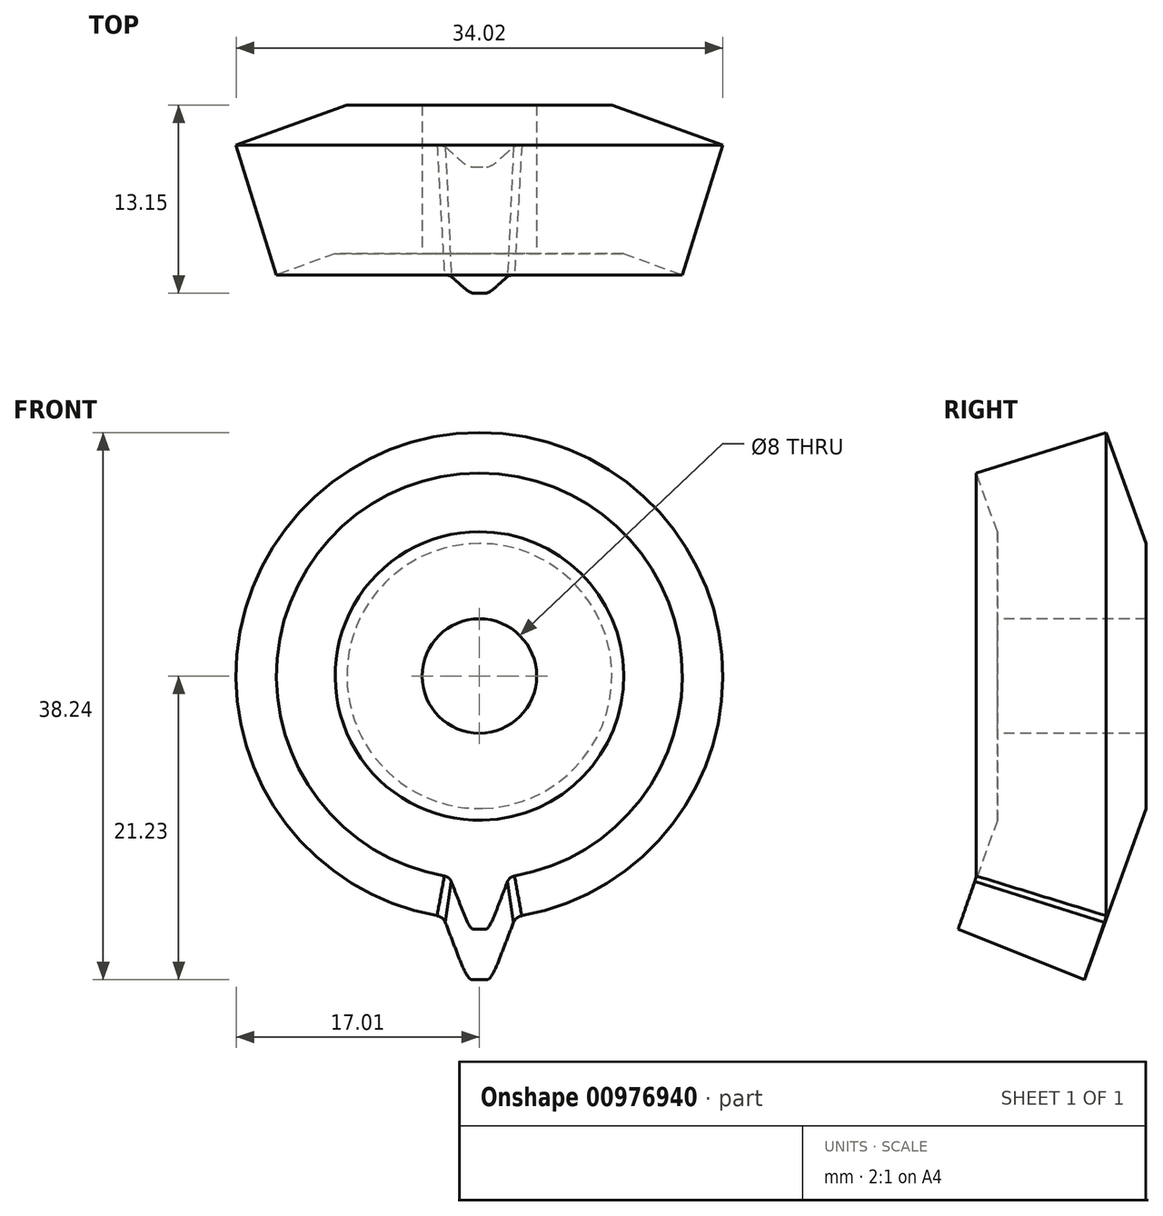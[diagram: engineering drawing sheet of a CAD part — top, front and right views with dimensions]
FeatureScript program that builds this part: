
annotation { "Feature Type Name" : "Feature", "Feature Type Description" : "" }
export const myFeature = defineFeature(function(context is Context, id is Id, definition is map)
    precondition{}
    {
        {
            var Q0;
            Q0=qCreatedBy(makeId("Right.planeOp"),FACE);
            var sketch = newSketch(context, id + "F0", { "sketchPlane" : qUnion([Q0])});
            skLineSegment(sketch, "E0", {"start": v(0, 0) * mm, "end": v(0, -10) * mm});
            skLineSegment(sketch, "E1", {"start": v(0, 0) * mm, "end": v(-57.43, 0) * mm, "construction": true});
            skLineSegment(sketch, "E2", {"start": v(0, 0) * mm, "end": v(3.61, 0) * mm, "construction": true});
            skLineSegment(sketch, "E3", {"start": v(3.61, 0) * mm, "end": v(-10.4, -38.83) * mm, "construction": true});
            skLineSegment(sketch, "E4", {"start": v(-57.43, 0) * mm, "end": v(-2.56, -17.09) * mm, "construction": true});
            skLineSegment(sketch, "E5", {"start": v(0, -10) * mm, "end": v(-2.56, -17.09) * mm});
            skLineSegment(sketch, "E6", {"start": v(-7.02, 0) * mm, "end": v(-12.12, -14.11) * mm, "construction": true});
            skLineSegment(sketch, "E7", {"start": v(-10.63, 0) * mm, "end": v(-10.63, -10) * mm, "construction": true});
            skLineSegment(sketch, "E8", {"start": v(-2.56, -17.09) * mm, "end": v(-12.12, -14.11) * mm});
            skLineSegment(sketch, "E9", {"start": v(-10.63, -10) * mm, "end": v(-10.63, 0) * mm});
            skLineSegment(sketch, "E10", {"start": v(-12.12, -14.11) * mm, "end": v(-10.63, -10) * mm});
            skLineSegment(sketch, "E11", {"start": v(0, 0) * mm, "end": v(-10.63, 0) * mm});
            skSolve(sketch);
        }
        {
            var Q0;
            Q0=makeQuery(id+"F0.imprint","IMPRINT",FACE,{"disambiguationData":[TD([[makeQuery(id+"F0.imprint","IMPRINT",EDGE,{"derivedFrom":sQuery(id+"F0.wireOp",EDGE,"E0")}),-1.0]])]});
            var Q1;
            Q1=sQuery(id+"F0.wireOp",EDGE,"E1");
            revolve(context, id + "F1", {"surfaceOperationType" : NewSurfaceOperationType.NEW, "entities" : qUnion([Q0]), "axis" : qUnion([Q1]), "revolveType" : RevolveType.FULL});
        }
        {
            var Q0;
            Q0=makeQuery(id+"F1.opRevolve","SWEPT_FACE",FACE,{"disambiguationData":[OSD([sQuery(id+"F0.wireOp",EDGE,"E9")])]});
            var sketch = newSketch(context, id + "F2", { "sketchPlane" : qUnion([Q0])});
            skCircle(sketch, "E12", {"center": v(0, 0) * mm, "radius": 4 * mm});
            skSolve(sketch);
        }
        {
            var Q0;
            Q0=makeQuery(id+"F2.imprint","IMPRINT",FACE,{"disambiguationData":[TD([[makeQuery(id+"F2.imprint","IMPRINT",EDGE,{"derivedFrom":sQuery(id+"F2.wireOp",EDGE,"E12")}),1.0]])]});
            extrude(context, id + "F3", {"entities" : qUnion([Q0]), "operationType" : NewBodyOperationType.REMOVE, "endBound" : BoundingType.THROUGH_ALL, "oppositeDirection" : true, "depth" : 25 * mm, "offsetDistance" : 25 * mm});
        }
        {
            var Q0;
            Q0=qCreatedBy(makeId("Right.planeOp"),FACE);
            var sketch = newSketch(context, id + "F4", { "sketchPlane" : qUnion([Q0])});
            skLineSegment(sketch, "E13.0", {"start": v(-2.56, 17.09) * mm, "end": v(-2.56, -17.09) * mm, "construction": true});
            skLineSegment(sketch, "E13.1", {"start": v(-12.12, 14.11) * mm, "end": v(-12.12, -14.11) * mm, "construction": true});
            skLineSegment(sketch, "E14", {"start": v(-12.12, -14.11) * mm, "end": v(-2.56, -17.09) * mm});
            skLineSegment(sketch, "E15.0", {"start": v(0, 10) * mm, "end": v(0, -10) * mm});
            skLineSegment(sketch, "E16", {"start": v(-2.56, -17.09) * mm, "end": v(0, -10) * mm});
            skLineSegment(sketch, "E17.0", {"start": v(-10.63, 10) * mm, "end": v(-10.63, -10) * mm});
            skLineSegment(sketch, "E18", {"start": v(-12.12, -14.11) * mm, "end": v(-10.63, -10) * mm});
            skSolve(sketch);
        }
        {
            var Q0;
            Q0=sQuery(id+"F4.wireOp",EDGE,"E16");
            cPlane(context, id + "F5", {"entities" : qUnion([Q0]), "cplaneType" : CPlaneType.LINE_ANGLE, "offset" : 25 * mm, "angle" : 90 * degree, "width" : 150 * mm, "height" : 150 * mm});
        }
        {
            var Q0;
            Q0=qCreatedBy(id+"F5.planeOp",FACE);
            var sketch = newSketch(context, id + "F6", { "sketchPlane" : qUnion([Q0])});
            skEllipticalArc(sketch, "E19.0", {});
            skLineSegment(sketch, "E20", {"start": v(0, -16.94) * mm, "end": v(0, -21.44) * mm, "construction": true});
            skPoint(sketch, "E21", {"position": v(0, -19.44) * mm});
            skLineSegment(sketch, "E22", {"start": v(1.57, -19.44) * mm, "end": v(1.57, -19.44) * mm});
            skLineSegment(sketch, "E23", {"start": v(-1.57, -19.44) * mm, "end": v(-1.57, -21.5) * mm, "construction": true});
            skLineSegment(sketch, "E24", {"start": v(1.57, -19.44) * mm, "end": v(1.57, -21.44) * mm, "construction": true});
            skLineSegment(sketch, "E25", {"start": v(0.84, -21.44) * mm, "end": v(1.57, -19.44) * mm, "construction": true});
            skLineSegment(sketch, "E26", {"start": v(-0.84, -21.44) * mm, "end": v(-1.57, -19.44) * mm, "construction": true});
            skLineSegment(sketch, "E27", {"start": v(0.84, -21.44) * mm, "end": v(0.5, -21.44) * mm, "construction": true});
            skArc(sketch, "E28", {"start": v(-2.4, -17.19) * mm, "mid": v(-2.62, -16.86) * mm, "end": v(-2.98, -16.7) * mm});
            skArc(sketch, "E29", {"start": v(2.98, -16.7) * mm, "mid": v(2.62, -16.86) * mm, "end": v(2.4, -17.19) * mm});
            skLineSegment(sketch, "E30", {"start": v(1.57, -19.44) * mm, "end": v(-1.57, -19.44) * mm, "construction": true});
            skLineSegment(sketch, "E31", {"start": v(-1.57, -19.44) * mm, "end": v(-2.4, -17.19) * mm});
            skLineSegment(sketch, "E32", {"start": v(-0.5, -21.44) * mm, "end": v(-0.84, -21.44) * mm, "construction": true});
            skLineSegment(sketch, "E33", {"start": v(0.5, -21.44) * mm, "end": v(-0.5, -21.44) * mm});
            skFitSpline(sketch, "E34", {"points": [v(-1.57, -19.44) * mm, v(-0.5, -21.44) * mm], "startDerivative": vector(1.1, -3) * mm, "endDerivative": vector(1.03, 0) * mm});
            skFitSpline(sketch, "E35", {"points": [v(1.57, -19.44) * mm, v(0.5, -21.44) * mm], "startDerivative": vector(-1.1, -3) * mm, "endDerivative": vector(-1.03, 0) * mm});
            skLineSegment(sketch, "E36", {"start": v(1.57, -19.44) * mm, "end": v(2.4, -17.19) * mm});
            skLineSegment(sketch, "E37", {"start": v(0.84, -21.44) * mm, "end": v(1.57, -21.44) * mm, "construction": true});
            skLineSegment(sketch, "E38", {"start": v(-1.57, -19.44) * mm, "end": v(-1.57, -19.44) * mm});
            const initialGuessF6  = {"E19.0": [0, -0.0008694535613683707, 1, 0, 0.017088939192445675, 0.016073068969560622, 4.537043889001193, 4.887734071768186]};
            skSetInitialGuess(sketch, initialGuessF6);
            skSolve(sketch);
        }
        {
            var Q0;
            Q0=sQuery(id+"F4.wireOp",EDGE,"E18");
            cPlane(context, id + "F7", {"entities" : qUnion([Q0]), "cplaneType" : CPlaneType.LINE_ANGLE, "offset" : 25 * mm, "angle" : 90 * degree, "width" : 150 * mm, "height" : 150 * mm});
        }
        {
            var Q0;
            Q0=qCreatedBy(id+"F7.planeOp",FACE);
            var sketch = newSketch(context, id + "F8", { "sketchPlane" : qUnion([Q0])});
            skEllipticalArc(sketch, "E39.0", {});
            skLineSegment(sketch, "E40", {"start": v(0, -17.39) * mm, "end": v(0, -21.1) * mm, "construction": true});
            skLineSegment(sketch, "E41", {"start": v(-1.3, -19.39) * mm, "end": v(1.3, -19.39) * mm, "construction": true});
            skLineSegment(sketch, "E42", {"start": v(-1.3, -19.39) * mm, "end": v(-1.3, -22.8) * mm, "construction": true});
            skLineSegment(sketch, "E43", {"start": v(1.3, -19.39) * mm, "end": v(1.3, -22.76) * mm, "construction": true});
            skLineSegment(sketch, "E44", {"start": v(0.68, -21.1) * mm, "end": v(1.3, -19.39) * mm, "construction": true});
            skLineSegment(sketch, "E45", {"start": v(-0.68, -21.1) * mm, "end": v(-1.3, -19.39) * mm, "construction": true});
            skLineSegment(sketch, "E46", {"start": v(-0.68, -21.1) * mm, "end": v(-0.4, -21.1) * mm, "construction": true});
            skArc(sketch, "E47", {"start": v(2.44, -17.19) * mm, "mid": v(2.14, -17.33) * mm, "end": v(1.95, -17.6) * mm});
            skArc(sketch, "E48", {"start": v(-1.95, -17.6) * mm, "mid": v(-2.14, -17.33) * mm, "end": v(-2.44, -17.19) * mm});
            skPoint(sketch, "E49.orphan", {"position": v(0, -19.39) * mm});
            skLineSegment(sketch, "E50", {"start": v(-0.4, -21.1) * mm, "end": v(0.4, -21.1) * mm});
            skLineSegment(sketch, "E51", {"start": v(0.4, -21.1) * mm, "end": v(0.68, -21.1) * mm, "construction": true});
            skLineSegment(sketch, "E52", {"start": v(-1.3, -19.39) * mm, "end": v(-1.95, -17.6) * mm});
            skLineSegment(sketch, "E53", {"start": v(1.3, -19.39) * mm, "end": v(1.95, -17.6) * mm});
            skFitSpline(sketch, "E54", {"points": [v(-1.3, -19.39) * mm, v(-0.4, -21.1) * mm], "startDerivative": vector(0.94, -2.57) * mm, "endDerivative": vector(0.83, 0) * mm});
            skFitSpline(sketch, "E55", {"points": [v(1.3, -19.39) * mm, v(0.4, -21.1) * mm], "startDerivative": vector(-0.94, -2.57) * mm, "endDerivative": vector(-0.83, 0) * mm});
            const initialGuessF8  = {"E39.0": [0, -0.00411549861527232, 1, 0, 0.014112445312662834, 0.013273515944152619, 4.538532018722645, 4.886245942046733]};
            skSetInitialGuess(sketch, initialGuessF8);
            skSolve(sketch);
        }
        {
            var Q1;
            Q1=makeQuery(id+"F6.imprint","IMPRINT",FACE,{"disambiguationData":[TD([[makeQuery(id+"F6.imprint","IMPRINT",EDGE,{"derivedFrom":sQuery(id+"F6.wireOp",EDGE,"E19.0")}),-1.0]])]});
            var Q2;
            Q2=makeQuery(id+"F8.imprint","IMPRINT",FACE,{"disambiguationData":[TD([[makeQuery(id+"F8.imprint","IMPRINT",EDGE,{"derivedFrom":sQuery(id+"F8.wireOp",EDGE,"E39.0")}),-1.0]])]});
            loft(context, id + "F9", {"operationType" : NewBodyOperationType.ADD, "sheetProfilesArray" : [{ "sheetProfileEntities" : qUnion([Q1]) }, { "sheetProfileEntities" : qUnion([Q2]) }]});
        }
        {
            var Q0;
            Q0=qCreatedBy(makeId("Right.planeOp"),FACE);
            var sketch = newSketch(context, id + "F10", { "sketchPlane" : qUnion([Q0])});
            skLineSegment(sketch, "E56", {"start": v(0, 0) * mm, "end": v(0, -10) * mm, "construction": true});
            skLineSegment(sketch, "E57", {"start": v(0, 0) * mm, "end": v(-57.43, 0) * mm, "construction": true});
            skLineSegment(sketch, "E58", {"start": v(0, 0) * mm, "end": v(3.61, 0) * mm, "construction": true});
            skLineSegment(sketch, "E59", {"start": v(3.61, 0) * mm, "end": v(-10.4, -38.83) * mm, "construction": true});
            skLineSegment(sketch, "E60", {"start": v(-57.43, 0) * mm, "end": v(-2.56, -17.09) * mm, "construction": true});
            skLineSegment(sketch, "E61", {"start": v(0, -10) * mm, "end": v(-2.56, -17.09) * mm, "construction": true});
            skLineSegment(sketch, "E62", {"start": v(-7.02, 0) * mm, "end": v(-12.12, -14.11) * mm, "construction": true});
            skLineSegment(sketch, "E63", {"start": v(-10.63, 0) * mm, "end": v(-10.63, -10) * mm, "construction": true});
            skLineSegment(sketch, "E64", {"start": v(-2.56, -17.09) * mm, "end": v(-12.12, -14.11) * mm, "construction": true});
            skLineSegment(sketch, "E65", {"start": v(-10.63, -10) * mm, "end": v(-10.63, 0) * mm, "construction": true});
            skLineSegment(sketch, "E66", {"start": v(-12.12, -14.11) * mm, "end": v(-10.63, -10) * mm, "construction": true});
            skLineSegment(sketch, "E67", {"start": v(0, 0) * mm, "end": v(-10.63, 0) * mm, "construction": true});
            skLineSegment(sketch, "E68", {"start": v(1.44, -6) * mm, "end": v(-4.7, -23.02) * mm, "construction": true});
            skLineSegment(sketch, "E69", {"start": v(-4.7, -23.02) * mm, "end": v(0, -24.72) * mm, "construction": true});
            skLineSegment(sketch, "E70", {"start": v(0, -24.72) * mm, "end": v(6.15, -7.7) * mm, "construction": true});
            skLineSegment(sketch, "E71", {"start": v(6.15, -7.7) * mm, "end": v(1.44, -6) * mm, "construction": true});
            skLineSegment(sketch, "E72", {"start": v(1.44, -6) * mm, "end": v(1.2, -5.92) * mm});
            skLineSegment(sketch, "E73", {"start": v(1.2, -5.92) * mm, "end": v(-4.94, -22.94) * mm});
            skLineSegment(sketch, "E74", {"start": v(-4.94, -22.94) * mm, "end": v(-4.7, -23.02) * mm});
            skLineSegment(sketch, "E75", {"start": v(1.44, -6) * mm, "end": v(1.82, -6.14) * mm});
            skLineSegment(sketch, "E76", {"start": v(1.82, -6.14) * mm, "end": v(-4.33, -23.16) * mm});
            skLineSegment(sketch, "E77", {"start": v(-4.33, -23.16) * mm, "end": v(-4.7, -23.02) * mm});
            skLineSegment(sketch, "E78", {"start": v(-10.63, -10) * mm, "end": v(-10.4, -10.08) * mm, "construction": true});
            skLineSegment(sketch, "E79", {"start": v(-10.4, -10.08) * mm, "end": v(-14.75, -22.13) * mm});
            skLineSegment(sketch, "E80", {"start": v(-14.75, -22.13) * mm, "end": v(-15.94, -21.76) * mm});
            skLineSegment(sketch, "E81", {"start": v(-15.94, -21.76) * mm, "end": v(-11.57, -9.66) * mm});
            skLineSegment(sketch, "E82", {"start": v(-11.57, -9.66) * mm, "end": v(-10.4, -10.08) * mm, "construction": true});
            skLineSegment(sketch, "E83", {"start": v(-10.4, -10.08) * mm, "end": v(-10.4, 0) * mm});
            skLineSegment(sketch, "E84", {"start": v(-10.63, 0) * mm, "end": v(-11.57, -9.66) * mm});
            skLineSegment(sketch, "E85", {"start": v(-10.4, 0) * mm, "end": v(-10.63, 0) * mm, "construction": true});
            skLineSegment(sketch, "E86", {"start": v(-10.4, 0) * mm, "end": v(-10.63, 0) * mm});
            skSolve(sketch);
        }
        {
            var Q0;
            Q0=makeQuery(id+"F10.imprint","IMPRINT",FACE,{"disambiguationData":[TD([[makeQuery(id+"F10.imprint","IMPRINT",EDGE,{"derivedFrom":sQuery(id+"F10.wireOp",EDGE,"E72")}),1.0]])]});
            var Q1;
            Q1=makeQuery(id+"F10.imprint","IMPRINT",FACE,{"disambiguationData":[TD([[makeQuery(id+"F10.imprint","IMPRINT",EDGE,{"derivedFrom":sQuery(id+"F10.wireOp",EDGE,"E79")}),-1.0]])]});
            var Q2;
            Q2=makeQuery(id+"F1.opRevolve","SWEPT_EDGE",EDGE,{"disambiguationData":[OSD([sQuery(id+"F0.wireOp",EDGE,"E0"),sQuery(id+"F0.wireOp",EDGE,"E5")])]});
            revolve(context, id + "F11", {"operationType" : NewBodyOperationType.REMOVE, "surfaceOperationType" : NewSurfaceOperationType.NEW, "entities" : qUnion([Q0, Q1]), "axis" : qUnion([Q2]), "revolveType" : RevolveType.FULL, "oppositeDirection" : true});
        }
    });
